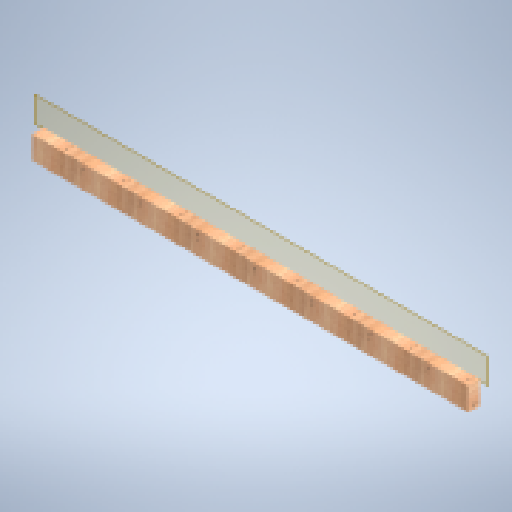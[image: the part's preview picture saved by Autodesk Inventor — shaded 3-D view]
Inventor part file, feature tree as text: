
AUTODESK INVENTOR PART (.ipt)
format: ipt  version: 2025 (Build 290162000, 162)  size: 143,872 bytes
history: native  units: in
note: dims shown in document units (in); Inventor stores cm internally (conversion verified against a paired STEP export)
features: other x7, reference x6, plane x1, extrude x1, sketch x1
ambient origin geometry x8: Origin, YZ Plane, XZ Plane, XY Plane, X Axis, Y Axis, Z Axis, Center Point
bodies: Solid1 (feature_tree)
feature tree (16):
  plane  "Work Plane1"
  extrude  "Extrusion1"  Depth=2.0in TaperAngle=0.0deg
  sketch  "Sketch1"  dims[d0=4.0in d1=2.0in d2=0.0in]
  reference  "Reference1"
  reference  "Reference2"
  reference  "Reference3"
  reference  "Reference4"
  reference  "Reference5"
  reference  "Reference6"
  other  "<userpath>\Documents\GitHub\USCTigerBurn24\v2\Tiger.iam"
  other  "Tiger.iam"
  other  "2x4x72_MIR:7"
  other  "2x4x48_MIR:8"
  other  "2x4x72_MIR:3"
  other  "2x4x48_MIR:12"
  other  "2x4x48_MIR:14"
